# Revit family: 2014-ES_Puerta-Enrollable-AEPA
name_source: partatom
category: Puertas
revit_build: Autodesk Revit 2014 (Build: 20130308_1515(x64)
units: mm (PartAtom-declared; Revit-internal decimal feet)

## types (1)
- Puerta Enrollable 3000 x 3000 mm
    Altura = 3000 mm  [stored 9.84252 ft]
    Altura Control = 3000 mm  [stored 9.84252 ft]
    Altura Real Hueco = 3347 mm
    Aluminio = Lamas aluminio- Puerta Generica- AEPA
    Anchura = 3000 mm  [stored 9.84252 ft]
    Anchura Real Hueco = 3210 mm
    Anchura de marco = 75 mm  [stored 0.246063 ft]
    Asociación- AEPA = http://www.aepa.ws
    Bimetica = www.bimetica.com
    Cierre de muro = Por anfitrión
    Colección = Biblioteca BIM AEPA
    Creado por = Bimetica Parametric Design Services S.L.
    Descripción = Puerta Enrollable Genérica AEPA
    Desfase Exterior = 0 mm  [stored 0 ft]
    Desfase Interior = 0 mm  [stored 0 ft]
    Estructura = Aluminio- Puerta Generica- AEPA
    Fabricante - CONTROLSA = http://www.controlsa.com
    Fabricante - ROLLTORE PORTIS = http://www.portis.es
    Fecha Revisión de Contenido = 22/12/2014
    Fecha de Caducidad de Información = 01/01/2016
    Función = Interior
    Goma = Gomas- Puerta Generica- AEPA
    Grosor del marco = 65 mm
    Información Técnica = http://bimetica.com
    Masterformat Código = 08 11 66.23
    Masterformat Descripción = Aluminum Screen Doors and Frames
    Media Lama = 1519 mm
    Modelo = Genérico AEPA
    Numero de Lamas = 30
    Numero de Perforaciones por Lama = 14
    Omniclass Código = 23-17 11 13 13 11
    Omniclass Título = Aluminum Screen Doors
    Proyección marco ext. = 25 mm  [stored 0.082021 ft]
    Proyección marco int. = 25 mm  [stored 0.082021 ft]
    UNSPSC Categoría = Rolling garage door
    UNSPSC Código = 30172108
    URL = http://www.aepa.ws
    Uniclass 2.0 Código = 25-30-20-74
    Uniclass 2.0 Descripción = Roller shutter doorset systems

note: [stored X ft] marks values corroborated as IEEE doubles in the binary element streams (Revit-internal decimal feet)

## geometry (parser evidence)
native form markers: Blend x2, Sweep x3
no freeform markers — native parametric forms only
